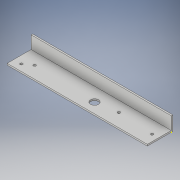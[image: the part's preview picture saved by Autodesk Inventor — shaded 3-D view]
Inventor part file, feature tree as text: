
AUTODESK INVENTOR PART (.ipt)
format: ipt  version: 2018 (Build 220112000, 112)  size: 143,872 bytes
history: native  units: in
note: dims shown in document units (in); Inventor stores cm internally (conversion verified against a paired STEP export)
features: other x8, sketch x7, reference x5, extrude x2
ambient origin geometry x8: Origin, YZ Plane, XZ Plane, XY Plane, X Axis, Y Axis, Z Axis, Center Point
bodies: Solid1 (feature_tree)
feature tree (22):
  other  "angle iron with  holes 2.ipt"
  sketch  "Sketch5"  dims[d12=0.2031in]
  sketch  "Sketch6"  dims[d13=1.0in d14=0.0in]
  extrude  "Extrusion3"  Depth=0.3937in
  extrude  "Extrusion4"  Depth=1.045in
  other  "Solid1::angle iron with  holes 2.ipt"
  other  "TaggingFeature1"
  sketch  "Sketch1"  dims[d0=0.3937in d2=0.2031in]
  sketch  "Sketch2"  dims[d3=0.2031in d6=1.045in]
  sketch  "Sketch3"  dims[d7=3.3in]
  sketch  "Sketch4"  dims[d11=1.045in]
  reference  "Reference1"
  reference  "Reference2"
  reference  "Reference3"
  sketch  "Sketch7"  dims[d15=0.796in d16=0.796in d17=0.625in d18=1.0in d19=0.0in]
  reference  "Reference4"
  reference  "Reference5"
  other  "USE THIS main gripper assembly CLOSED version.iam"
  other  "motor assembly_MIR:1"
  other  "VersaPlanetary_v2_Single_Stage_10_1_with_775_Series_MIR:1"
  other  "eye screw stand-in:1"
  other  "base mount:1"
